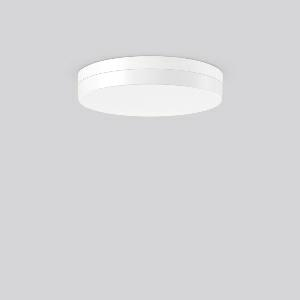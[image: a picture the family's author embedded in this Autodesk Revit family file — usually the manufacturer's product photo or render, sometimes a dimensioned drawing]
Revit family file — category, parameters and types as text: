
# Revit family: flat_slim_round_312675_002_19_1c71
name_source: partatom
category: Lighting Fixtures
units: mm (PartAtom-declared; Revit-internal decimal feet)

## family parameters
Cut with Voids When Loaded = No
Host = Face
Light Source = No
Part Type = Normal
Room Calculation Point = No
Round Connector Dimension = Use Diameter
Shared = No

## types (1)
- MultiLumen 1 830 (1 x LED Modul 830, 2450 lm, 3000)
    Apparent Load = 25 VA
    CIE Flux Codes = 40 70 90 84 100
    Color Rendering = 80
    Color Temperature = 3000
    Default Elevation = 1800 mm
    Height = 75 mm
    Lamp = 1 x LED Modul 830
    Lamp Light Flux = 2450 lm
    Lamp count = 1
    Length = 400 mm
    Lifetime = 50000 h
    Luminous efficacy = 98 lm/W
    Manufacturer = RZB
    ModVariant = No
    Model = 312675.002.19
    Mounting Place = Ceiling
    Mounting Type = Surface mounted
    Number of Poles = 1
    OnlyDefault = Yes
    Power Factor = 1
    Product Name = FLAT SLIM round
    Product group = Surface mounted ceiling and wall luminaires
    ProductGroupID = 305
    Protection Class = Protection class I
    Protection Degree = Degree of protection
    RLX_Detail_Level = 1
    RLX_Emergency_Light_Flux = 0 lm
    RLX_Emergency_Type = 0
    RLX_Emergency_Type_DB = No
    RlxData = <blob elided: 20445 chars, md5=32763d3d>
    Socket = socket
    Standby Power = 0 W
    System Light Flux = 2450 lm
    System Power = 25 W
    Type Comments = MultiLumen 1 830
    Type Image = 312631.002.jpg
    URL = http://relux.com
    VarID = multilumen_1_830
    Voltage = 0 V
    Weight = 0.00 kg
    Width = 0 mm  [stored 0 ft]

note: [stored X ft] marks values corroborated as IEEE doubles in the binary element streams (Revit-internal decimal feet)

## geometry (parser evidence)
native form markers: Blend x4, Sweep x13
no freeform markers — native parametric forms only
